# Revit family: ITK_Стенка задняя для шкафа WE шириной 600 мм_6U-18U
name_source: partatom
category: Обобщенные модели
units: mm (PartAtom-declared; Revit-internal decimal feet)

## family parameters
Всегда вертикально = Да
Может служить основой для арматурных стержней = Нет
На основе рабочей плоскости = Нет
Общий = Нет
При загрузке вырезать с полостями = Нет
Размер круглого соединителя = Использовать диаметр
Тип детали = Нормальный
Точка расчета площади = Нет

## types (9) — shared parameters
ADSK_URL страницы изделия = https://www.itk-group.ru
ADSK_Версия Revit = 2019
ADSK_Версия семейства = 1.0
ADSK_Группирование = I. ЩИТЫ И ПУЛЬТЫ
ADSK_Единица измерения = шт
ADSK_Завод-изготовитель = IEK
ADSK_Марка = LINEA WE
ADSK_Материал наименование = Листовая сталь
IEK_URL = https://www.itk-group.ru
IEK_Описание = Широкий ассортимент видов и исполнений. Удобны в монтаже и эксплуатации. Соответствие российским и международным стандартам. Все стенки идут с крепежом. Поставляются в качественной надежной упаковке.
KSI_CMa_Строительные материалы = 10.03.02.06
KSI_CPr_Строительные изделия = 61.1.04.08
URL = https://www.iek.ru
Изготовитель = ITK
Ширина = 600 мм

## per-type parameters (varying)
| type | ADSK_Код изделия | ADSK_Масса | ADSK_Наименование | IEK_Цена за единицу | Высота | Материал |
| В254_Серый | LWE3-06U-600-MW | 1 | ITK Стенка задняя для шкафа WE 6U шириной 600мм серая | 499.42 | 254 мм | Окраска - RAL 7035 |
| В384_Серый | LWE3-09U-600-MW | 1.5 | ITK Стенка задняя для шкафа WE 9U шириной 600мм серая | 663.32 | 384 мм | Окраска - RAL 7035 |
| В519_Серый | LWE3-12U-600-MW | 1.98 | ITK Стенка задняя для шкафа WE 12U шириной 600мм серая | 829.63 | 519 мм | Окраска - RAL 7035 |
| В649_Серый | LWE3-15U-600-MW | 2.45 | ITK Стенка задняя для шкафа WE 15U шириной 600мм серая | 942.29 | 649 мм | Окраска - RAL 7035 |
| В784_Серый | LWE3-18U-600-MW | 2.95 | ITK Стенка задняя для шкафа WE 18U шириной 600мм серая | 1067.26 | 784 мм | Окраска - RAL 7035 |
| В254_Черный | LWE5-06U-600-MW | 1 | ITK Стенка задняя для шкафа WE 6U шириной 600мм черная | 499.42 | 254 мм | Окраска - RAL 9005 |
| В384_Черный | LWE5-09U-600-MW | 1.5 | ITK Стенка задняя для шкафа WE 9U шириной 600мм черная | 663.32 | 384 мм | Окраска - RAL 9005 |
| В519_Черный | LWE5-12U-600-MW | 1.98 | ITK Стенка задняя для шкафа WE 12U шириной 600мм черная | 829.63 | 519 мм | Окраска - RAL 9005 |
| В649_Черный | LWE5-15U-600-MW | 2.45 | ITK Стенка задняя для шкафа WE 15U шириной 600мм черная | 942.29 | 649 мм | Окраска - RAL 9005 |
